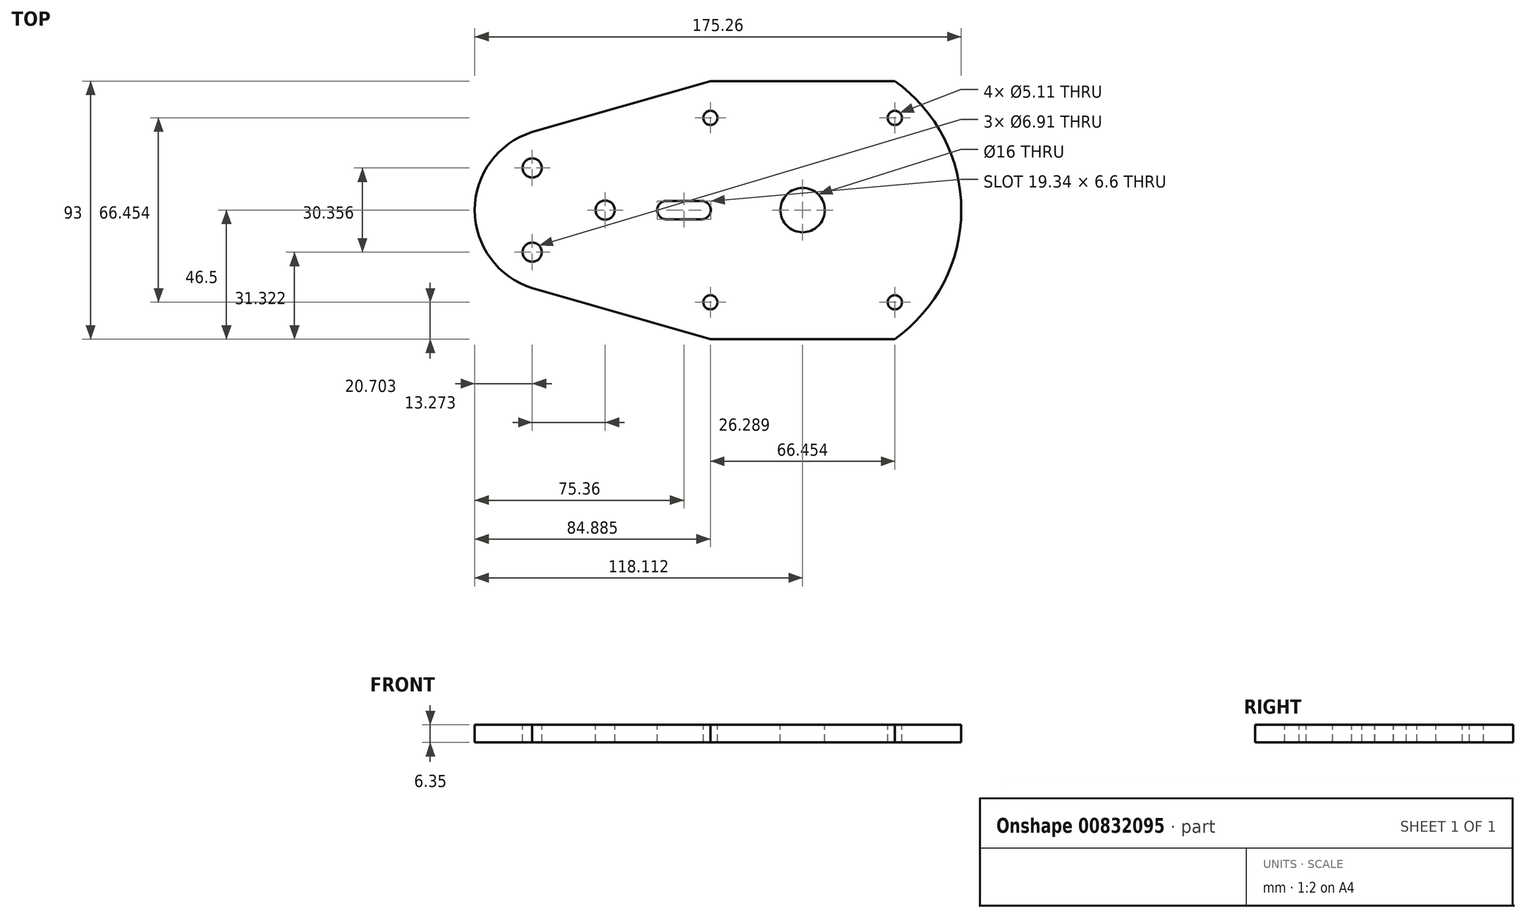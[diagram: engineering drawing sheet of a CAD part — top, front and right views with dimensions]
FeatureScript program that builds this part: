
annotation { "Feature Type Name" : "Feature", "Feature Type Description" : "" }
export const myFeature = defineFeature(function(context is Context, id is Id, definition is map)
    precondition{}
    {
        {
            var Q0;
            Q0=qCreatedBy(makeId("Top.planeOp"),FACE);
            var sketch = newSketch(context, id + "F0", { "sketchPlane" : qUnion([Q0])});
            skLineSegment(sketch, "E0", {"start": v(0, 0) * mm, "end": v(-58.93, 0) * mm, "construction": true});
            skPoint(sketch, "E1", {"position": v(-29.46, 0) * mm});
            skCircle(sketch, "E2", {"center": v(-29.46, 0) * mm, "radius": 29.46 * mm, "construction": true});
            skCircle(sketch, "E3", {"center": v(-29.46, 0) * mm, "radius": 17.53 * mm, "construction": true});
            skPoint(sketch, "E4", {"position": v(59.18, 0) * mm});
            skPoint(sketch, "E5", {"position": v(-11.94, 0) * mm});
            skCircle(sketch, "E6", {"center": v(59.18, 0) * mm, "radius": 19.05 * mm, "construction": true});
            skCircle(sketch, "E7", {"center": v(59.18, 0) * mm, "radius": 31.75 * mm, "construction": true});
            skCircle(sketch, "E8", {"center": v(-11.94, 0) * mm, "radius": 3.45 * mm});
            skCircle(sketch, "E9", {"center": v(-29.46, 0) * mm, "radius": 10.16 * mm, "construction": true});
            skArc(sketch, "E10", {"start": v(92.4, -46.5) * mm, "mid": v(116.33, 0) * mm, "end": v(92.4, 46.5) * mm, "construction": true});
            skPoint(sketch, "E11", {"position": v(59.18, 57.15) * mm});
            skPoint(sketch, "E12", {"position": v(59.18, -57.15) * mm});
            skCircle(sketch, "E13", {"center": v(59.18, 0) * mm, "radius": 47 * mm, "construction": true});
            skLineSegment(sketch, "E14", {"start": v(59.18, 0) * mm, "end": v(99.6, 40.41) * mm, "construction": true});
            skCircle(sketch, "E15", {"center": v(92.4, 33.23) * mm, "radius": 2.55 * mm});
            skCircle(sketch, "E16", {"center": v(59.18, 0) * mm, "radius": 8 * mm});
            skPoint(sketch, "E17", {"position": v(25.96, 46.5) * mm});
            skPoint(sketch, "E18", {"position": v(25.96, -46.5) * mm});
            skLineSegment(sketch, "E19", {"start": v(25.96, 46.5) * mm, "end": v(92.4, 46.5) * mm});
            skLineSegment(sketch, "E20", {"start": v(25.96, -46.5) * mm, "end": v(92.4, -46.5) * mm});
            skArc(sketch, "E21.converted", {"start": v(92.4, 46.5) * mm, "mid": v(2.03, 0) * mm, "end": v(92.4, -46.5) * mm, "construction": true});
            skLineSegment(sketch, "E22", {"start": v(59.18, 0) * mm, "end": v(99.6, -40.41) * mm, "construction": true});
            skCircle(sketch, "E23", {"center": v(59.18, 0) * mm, "radius": 36.54 * mm, "construction": true});
            skCircle(sketch, "E24", {"center": v(59.18, 0) * mm, "radius": 49.24 * mm, "construction": true});
            skPoint(sketch, "E25", {"position": v(-38.23, 28.13) * mm});
            skLineSegment(sketch, "E26", {"start": v(25.96, 46.5) * mm, "end": v(-38.23, 28.13) * mm});
            skPoint(sketch, "E27", {"position": v(-38.23, -28.13) * mm});
            skLineSegment(sketch, "E28", {"start": v(25.96, -46.5) * mm, "end": v(-38.23, -28.13) * mm});
            skArc(sketch, "E29", {"start": v(-38.23, 28.13) * mm, "mid": v(-58.93, 0) * mm, "end": v(-38.23, -28.13) * mm});
            skCircle(sketch, "E30.1.0", {"center": v(-38.23, 15.18) * mm, "radius": 3.45 * mm});
            skCircle(sketch, "E30.2.0", {"center": v(-38.23, -15.18) * mm, "radius": 3.45 * mm});
            skLineSegment(sketch, "E31.1.0", {"start": v(22.8, -3.3) * mm, "end": v(10.06, -3.3) * mm});
            skLineSegment(sketch, "E31.1.2", {"start": v(22.8, 3.3) * mm, "end": v(10.06, 3.3) * mm});
            skCircle(sketch, "E32.1.0", {"center": v(25.96, 33.23) * mm, "radius": 2.55 * mm});
            skCircle(sketch, "E32.2.0", {"center": v(25.96, -33.23) * mm, "radius": 2.55 * mm});
            skCircle(sketch, "E32.3.0", {"center": v(92.4, -33.23) * mm, "radius": 2.55 * mm});
            skLineSegment(sketch, "E33", {"start": v(64.53, 0) * mm, "end": v(0, 0) * mm, "construction": true});
            skArc(sketch, "E34", {"start": v(10.06, 3.3) * mm, "mid": v(6.76, 0) * mm, "end": v(10.06, -3.3) * mm});
            skArc(sketch, "E35", {"start": v(22.8, 3.3) * mm, "mid": v(26.1, -0.02) * mm, "end": v(22.77, -3.3) * mm});
            skArc(sketch, "E36", {"start": v(92.4, -46.5) * mm, "mid": v(116.33, 0) * mm, "end": v(92.4, 46.5) * mm});
            skSolve(sketch);
        }
        {
            var Q0;
            Q0=makeQuery(id+"F0.imprint","IMPRINT",FACE,{"disambiguationData":[TD([[makeQuery(id+"F0.imprint","IMPRINT",EDGE,{"derivedFrom":sQuery(id+"F0.wireOp",EDGE,"E8")}),-1.0]])]});
            extrude(context, id + "F1", {"entities" : qUnion([Q0]), "oppositeDirection" : true, "depth" : 6.35 * mm, "offsetDistance" : 25.4 * mm});
        }
    });
